# Revit family: 44066
name_source: partatom
category: Lighting Fixtures
revit_build: Autodesk Revit 2018 (Build: 20170223_1515(x64)
units: mm (PartAtom-declared; Revit-internal decimal feet)

## family parameters
Cut with Voids When Loaded = No
Host = Face
Light Source = Yes
OmniClass Number = 23.80.70.00
OmniClass Title = Lighting
Part Type = Normal
Room Calculation Point = No
Round Connector Dimension = Use Diameter
Shared = No

## types (1)
- 0044066 SPORTSBAY 12KLM 840 SS
    Apparent Load = 81 VA
    Assembly Code = D5020200
    AssetType = Fixed
    ClassificationName = Uniclass2015
    ClassificationValue = EF_70_80
    Color Filter = 16777215
    Cost = 0 $
    Default Elevation = 1219 mm
    Dimming Lamp Color Temperature Shift = <None>
    DocumentationLiterature = http://www.sylvania-lighting.com
    ElectricShockClassification = 156
    Emit Shape Visible in Rendering = No
    Emit from Circle Diameter = 610 mm
    Height = 76 mm
    IfcExportAs = Class I
    IfcExportType = IfcLightFixtureType
    ImpactProtectionIndex = IfcLightFixtureType
    IngressProtection = IfcLightFixtureType
    InputVoltage = 0
    LampColourRenderingIndex = 16500
    LampColourTemperature = LED
    Length = 1220 mm
    LightOutputRatio = LED
    LuminaireType = 0
    ManufacturerName = 156 lm/W
    Material = Feilo Sylvania
    Material_1_SYL = <By Category>
    Material_2_SYL = <By Category>
    Material_3_SYL = <By Category>
    Material_4_SYL = <By Category>
    Model = Sportsbay 12klm 840 SS
    ModelNumber = 0044066
    ModelReference = Sportsbay 12klm 840 SS
    Name = Sportsbay 12klm 840 SS
    NominalDepth = 320 mm
    NominalHeight = 76 mm
    NominalLength = 320 mm
    Photometric Web File = 0044066.IES
    PowerConsumption = Lighting
    PowerFactor = 0
    Tilt Angle = -90.00°
    Type Image = <None>
    TypeName = Sportsbay 12klm 840 SS
    URL = 0.95
    Voltage = 0 V
    WarrantyDescription = http://www.sylvania-lighting.com
    Width = 320 mm
    box length = 1160 mm

## geometry (parser evidence)
native form markers: Sweep x1
no freeform markers — native parametric forms only
